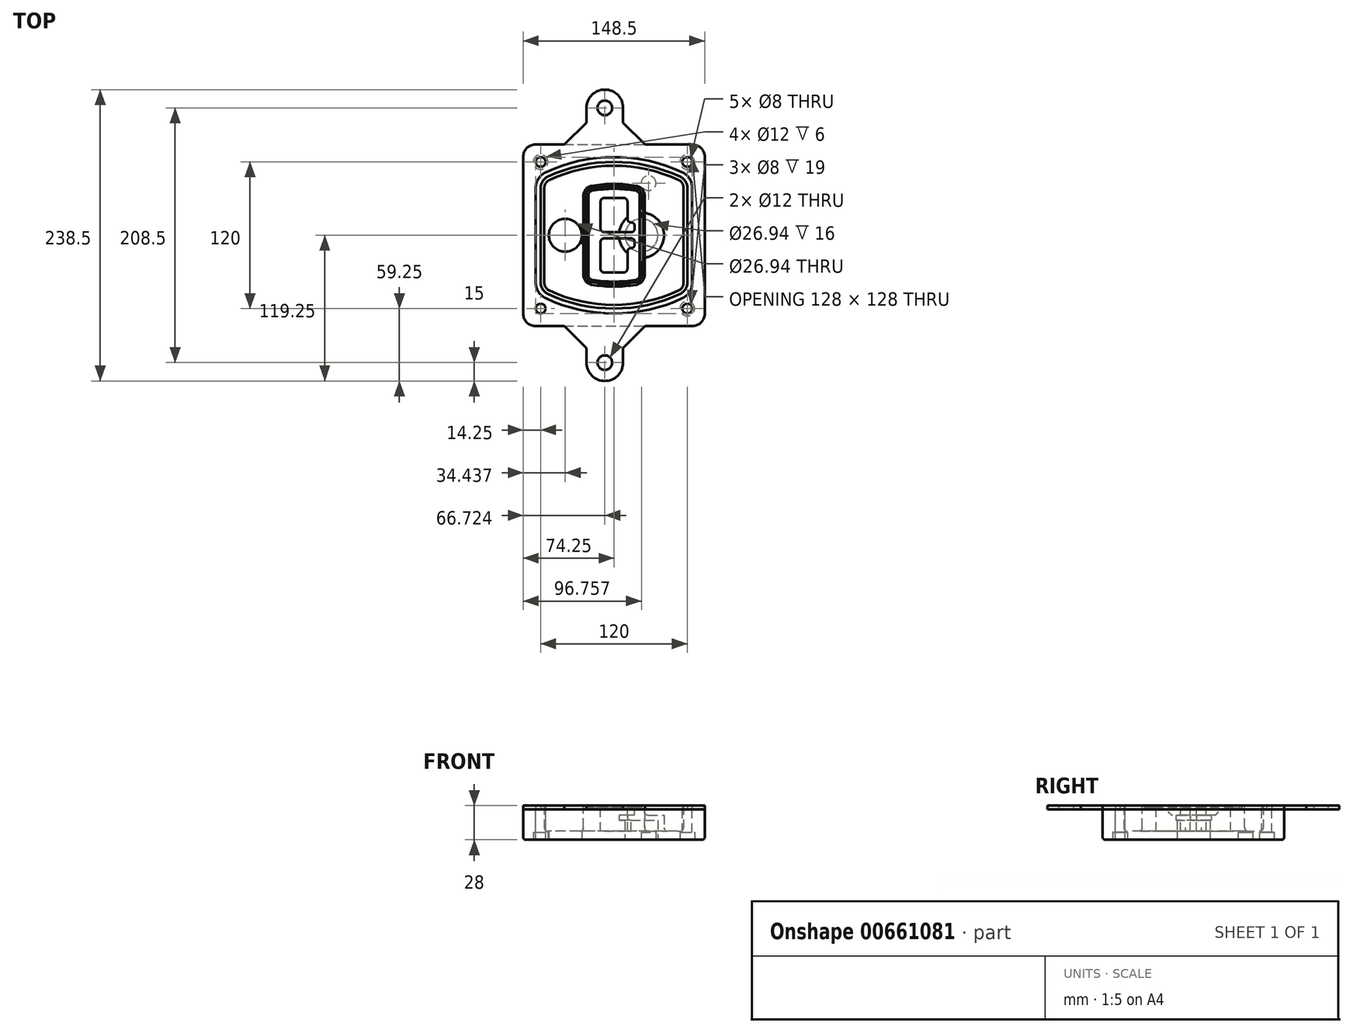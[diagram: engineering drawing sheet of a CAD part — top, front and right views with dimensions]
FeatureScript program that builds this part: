
annotation { "Feature Type Name" : "Feature", "Feature Type Description" : "" }
export const myFeature = defineFeature(function(context is Context, id is Id, definition is map)
    precondition{}
    {
        {
            var Q0;
            Q0=qCreatedBy(makeId("Top.planeOp"),FACE);
            var sketch = newSketch(context, id + "F0", { "sketchPlane" : qUnion([Q0])});
            skPoint(sketch, "E0.rect.middle", {"position": v(0, 0) * mm});
            skLineSegment(sketch, "E1.bottom", {"start": v(-64.25, -74.25) * mm, "end": v(64.25, -74.25) * mm});
            skLineSegment(sketch, "E1.top", {"start": v(-64.25, 74.25) * mm, "end": v(64.25, 74.25) * mm});
            skLineSegment(sketch, "E1.left", {"start": v(-74.25, -64.25) * mm, "end": v(-74.25, 64.25) * mm});
            skLineSegment(sketch, "E1.right", {"start": v(74.25, -64.25) * mm, "end": v(74.25, 64.25) * mm});
            skLineSegment(sketch, "E2", {"start": v(-74.25, 74.25) * mm, "end": v(74.25, -74.25) * mm, "construction": true});
            skLineSegment(sketch, "E3", {"start": v(74.25, 74.25) * mm, "end": v(-74.25, -74.25) * mm, "construction": true});
            skCircle(sketch, "E4", {"center": v(-60, 60) * mm, "radius": 4 * mm});
            skCircle(sketch, "E5", {"center": v(60, 60) * mm, "radius": 4 * mm});
            skCircle(sketch, "E6", {"center": v(60, -60) * mm, "radius": 4 * mm});
            skCircle(sketch, "E7", {"center": v(-60, -60) * mm, "radius": 4 * mm});
            skLineSegment(sketch, "E8", {"start": v(-60, 60) * mm, "end": v(60, 60) * mm, "construction": true});
            skLineSegment(sketch, "E9", {"start": v(60, 60) * mm, "end": v(60, -60) * mm, "construction": true});
            skLineSegment(sketch, "E10", {"start": v(60, -60) * mm, "end": v(-60, -60) * mm, "construction": true});
            skLineSegment(sketch, "E11", {"start": v(-60, -60) * mm, "end": v(-60, 60) * mm, "construction": true});
            skLineSegment(sketch, "E12", {"start": v(-60, 38.83) * mm, "end": v(-60, -38.83) * mm});
            skLineSegment(sketch, "E13", {"start": v(60, 38.83) * mm, "end": v(60, -38.83) * mm});
            skArc(sketch, "E14", {"start": v(54.26, 47.88) * mm, "mid": v(0, 60) * mm, "end": v(-54.26, 47.88) * mm});
            skArc(sketch, "E15", {"start": v(-54.26, -47.88) * mm, "mid": v(0, -60) * mm, "end": v(54.26, -47.88) * mm});
            skLineSegment(sketch, "E16", {"start": v(-60, 0) * mm, "end": v(60, 0) * mm, "construction": true});
            skPoint(sketch, "E17.visualSharp", {"position": v(-60, -45) * mm});
            skArc(sketch, "E17.filletArc", {"start": v(-60, -38.83) * mm, "mid": v(-58.44, -44.2) * mm, "end": v(-54.26, -47.88) * mm});
            skPoint(sketch, "E18.visualSharp", {"position": v(-60, 45) * mm});
            skArc(sketch, "E18.filletArc", {"start": v(-54.26, 47.88) * mm, "mid": v(-58.44, 44.2) * mm, "end": v(-60, 38.83) * mm});
            skPoint(sketch, "E19.visualSharp", {"position": v(60, 45) * mm});
            skArc(sketch, "E19.filletArc", {"start": v(60, 38.83) * mm, "mid": v(58.44, 44.2) * mm, "end": v(54.26, 47.88) * mm});
            skPoint(sketch, "E20.visualSharp", {"position": v(60, -45) * mm});
            skArc(sketch, "E20.filletArc", {"start": v(54.26, -47.88) * mm, "mid": v(58.44, -44.2) * mm, "end": v(60, -38.83) * mm});
            skPoint(sketch, "E21.visualSharp", {"position": v(-74.25, 74.25) * mm});
            skArc(sketch, "E21.filletArc", {"start": v(-64.25, 74.25) * mm, "mid": v(-71.32, 71.32) * mm, "end": v(-74.25, 64.25) * mm});
            skPoint(sketch, "E22.visualSharp", {"position": v(74.25, 74.25) * mm});
            skArc(sketch, "E22.filletArc", {"start": v(74.25, 64.25) * mm, "mid": v(71.32, 71.32) * mm, "end": v(64.25, 74.25) * mm});
            skPoint(sketch, "E23.visualSharp", {"position": v(74.25, -74.25) * mm});
            skArc(sketch, "E23.filletArc", {"start": v(64.25, -74.25) * mm, "mid": v(71.32, -71.32) * mm, "end": v(74.25, -64.25) * mm});
            skPoint(sketch, "E24.visualSharp", {"position": v(-74.25, -74.25) * mm});
            skArc(sketch, "E24.filletArc", {"start": v(-74.25, -64.25) * mm, "mid": v(-71.32, -71.32) * mm, "end": v(-64.25, -74.25) * mm});
            skArc(sketch, "E25.0", {"start": v(57, 38.83) * mm, "mid": v(55.9, 42.58) * mm, "end": v(52.98, 45.17) * mm});
            skLineSegment(sketch, "E25.1", {"start": v(57, 38.83) * mm, "end": v(57, -38.83) * mm});
            skArc(sketch, "E25.2", {"start": v(52.98, -45.17) * mm, "mid": v(55.9, -42.58) * mm, "end": v(57, -38.83) * mm});
            skArc(sketch, "E25.3", {"start": v(-52.98, -45.17) * mm, "mid": v(0, -57) * mm, "end": v(52.98, -45.17) * mm});
            skArc(sketch, "E25.4", {"start": v(-57, -38.83) * mm, "mid": v(-55.9, -42.58) * mm, "end": v(-52.98, -45.17) * mm});
            skArc(sketch, "E25.5", {"start": v(52.98, 45.17) * mm, "mid": v(0, 57) * mm, "end": v(-52.98, 45.17) * mm});
            skLineSegment(sketch, "E25.6", {"start": v(-57, 38.83) * mm, "end": v(-57, -38.83) * mm});
            skArc(sketch, "E25.7", {"start": v(-52.98, 45.17) * mm, "mid": v(-55.9, 42.58) * mm, "end": v(-57, 38.83) * mm});
            skArc(sketch, "E26.0", {"start": v(-55.96, 51.5) * mm, "mid": v(-61.82, 46.33) * mm, "end": v(-64, 38.83) * mm});
            skArc(sketch, "E26.1", {"start": v(55.96, 51.5) * mm, "mid": v(0, 64) * mm, "end": v(-55.96, 51.5) * mm});
            skArc(sketch, "E26.2", {"start": v(64, 38.83) * mm, "mid": v(61.82, 46.33) * mm, "end": v(55.96, 51.5) * mm});
            skLineSegment(sketch, "E26.3", {"start": v(64, 38.83) * mm, "end": v(64, -38.83) * mm});
            skArc(sketch, "E26.4", {"start": v(55.96, -51.5) * mm, "mid": v(61.82, -46.33) * mm, "end": v(64, -38.83) * mm});
            skLineSegment(sketch, "E26.5", {"start": v(-64, 38.83) * mm, "end": v(-64, -38.83) * mm});
            skArc(sketch, "E26.6", {"start": v(-55.96, -51.5) * mm, "mid": v(0, -64) * mm, "end": v(55.96, -51.5) * mm});
            skArc(sketch, "E26.7", {"start": v(-64, -38.83) * mm, "mid": v(-61.82, -46.33) * mm, "end": v(-55.96, -51.5) * mm});
            skLineSegment(sketch, "E27", {"start": v(-40.53, 74.25) * mm, "end": v(-22.53, 92.25) * mm});
            skLineSegment(sketch, "E28", {"start": v(25.47, 74.25) * mm, "end": v(7.47, 92.25) * mm});
            skLineSegment(sketch, "E29", {"start": v(7.47, 92.25) * mm, "end": v(7.47, 104.25) * mm});
            skLineSegment(sketch, "E30", {"start": v(-22.53, 92.25) * mm, "end": v(-22.53, 104.25) * mm});
            skArc(sketch, "E31", {"start": v(7.47, 104.25) * mm, "mid": v(-7.53, 119.25) * mm, "end": v(-22.53, 104.25) * mm});
            skCircle(sketch, "E32", {"center": v(-7.53, 104.25) * mm, "radius": 6 * mm});
            skLineSegment(sketch, "E33", {"start": v(-7.53, 104.25) * mm, "end": v(-7.53, 74.25) * mm, "construction": true});
            skLineSegment(sketch, "E34", {"start": v(-74.25, 0) * mm, "end": v(74.25, 0) * mm, "construction": true});
            skArc(sketch, "E35.MirrorCS", {"start": v(-64.25, -74.25) * mm, "mid": v(-71.32, -71.32) * mm, "end": v(-74.25, -64.25) * mm});
            skLineSegment(sketch, "E36.MirrorCS", {"start": v(-40.53, -74.25) * mm, "end": v(-22.53, -92.25) * mm});
            skLineSegment(sketch, "E37.MirrorCS", {"start": v(25.47, -74.25) * mm, "end": v(7.47, -92.25) * mm});
            skArc(sketch, "E38.MirrorCS", {"start": v(7.47, -104.25) * mm, "mid": v(-7.53, -119.25) * mm, "end": v(-22.53, -104.25) * mm});
            skCircle(sketch, "E39.MirrorC", {"center": v(-7.53, -104.25) * mm, "radius": 6 * mm});
            skLineSegment(sketch, "E40.MirrorCS", {"start": v(-7.53, -104.25) * mm, "end": v(-7.53, -74.25) * mm, "construction": true});
            skLineSegment(sketch, "E41.MirrorCS", {"start": v(-22.53, -92.25) * mm, "end": v(-22.53, -104.25) * mm});
            skLineSegment(sketch, "E42.MirrorCS", {"start": v(7.47, -92.25) * mm, "end": v(7.47, -104.25) * mm});
            skSolve(sketch);
        }
        {
            var Q0;
            Q0=makeQuery(id+"F0.imprint","IMPRINT",FACE,{"disambiguationData":[TD([[makeQuery(id+"F0.imprint","IMPRINT",EDGE,{"derivedFrom":sQuery(id+"F0.wireOp",EDGE,"E1.bottom")}),1.0]])]});
            var Q1;
            Q1=makeQuery(id+"F0.imprint","IMPRINT",FACE,{"disambiguationData":[TD([[makeQuery(id+"F0.imprint","IMPRINT",EDGE,{"derivedFrom":sQuery(id+"F0.wireOp",EDGE,"E12")}),1.0]])]});
            var Q2;
            Q2=makeQuery(id+"F0.imprint","IMPRINT",FACE,{"disambiguationData":[TD([[makeQuery(id+"F0.imprint","IMPRINT",EDGE,{"derivedFrom":sQuery(id+"F0.wireOp",EDGE,"E25.0")}),1.0]])]});
            var Q3;
            Q3=makeQuery(id+"F0.imprint","IMPRINT",FACE,{"disambiguationData":[TD([[makeQuery(id+"F0.imprint","IMPRINT",EDGE,{"derivedFrom":sQuery(id+"F0.wireOp",EDGE,"E12")}),-1.0]])]});
            extrude(context, id + "F1", {"entities" : qUnion([Q0, Q1, Q2, Q3]), "oppositeDirection" : true, "depth" : 25 * mm});
        }
        {
            var Q0;
            Q0=makeQuery(id+"F0.imprint","IMPRINT",FACE,{"disambiguationData":[TD([[makeQuery(id+"F0.imprint","IMPRINT",EDGE,{"derivedFrom":sQuery(id+"F0.wireOp",EDGE,"E12")}),1.0]])]});
            extrude(context, id + "F2", {"entities" : qUnion([Q0]), "operationType" : NewBodyOperationType.ADD, "depth" : 3 * mm});
        }
        {
            var Q0;
            Q0=makeQuery(id+"F0.imprint","IMPRINT",FACE,{"disambiguationData":[TD([[makeQuery(id+"F0.imprint","IMPRINT",EDGE,{"derivedFrom":sQuery(id+"F0.wireOp",EDGE,"E25.0")}),1.0]])]});
            extrude(context, id + "F3", {"entities" : qUnion([Q0]), "operationType" : NewBodyOperationType.REMOVE, "oppositeDirection" : true, "depth" : 18 * mm});
        }
        {
            var Q0;
            Q0=makeQuery(id+"F2.opExtrude","CAP_FACE",FACE,{"disambiguationData":[OSD([sQuery(id+"F0.wireOp",EDGE,"E12"),sQuery(id+"F0.wireOp",EDGE,"E13"),sQuery(id+"F0.wireOp",EDGE,"E14"),sQuery(id+"F0.wireOp",EDGE,"E15"),sQuery(id+"F0.wireOp",EDGE,"E17.filletArc"),sQuery(id+"F0.wireOp",EDGE,"E18.filletArc"),sQuery(id+"F0.wireOp",EDGE,"E19.filletArc"),sQuery(id+"F0.wireOp",EDGE,"E20.filletArc"),sQuery(id+"F0.wireOp",EDGE,"E25.0"),sQuery(id+"F0.wireOp",EDGE,"E25.1"),sQuery(id+"F0.wireOp",EDGE,"E25.2"),sQuery(id+"F0.wireOp",EDGE,"E25.3"),sQuery(id+"F0.wireOp",EDGE,"E25.4"),sQuery(id+"F0.wireOp",EDGE,"E25.5"),sQuery(id+"F0.wireOp",EDGE,"E25.6"),sQuery(id+"F0.wireOp",EDGE,"E25.7")])],"isStart":false});
            var sketch = newSketch(context, id + "F4", { "sketchPlane" : qUnion([Q0])});
            skArc(sketch, "E43.0", {"start": v(-18.34, -40.45) * mm, "mid": v(0, -42) * mm, "end": v(18.34, -40.45) * mm});
            skArc(sketch, "E44.0", {"start": v(18.34, 40.45) * mm, "mid": v(0, 42) * mm, "end": v(-18.34, 40.45) * mm});
            skLineSegment(sketch, "E45", {"start": v(-25, 32.57) * mm, "end": v(-25, -32.57) * mm});
            skLineSegment(sketch, "E46", {"start": v(25, 32.57) * mm, "end": v(25, -32.57) * mm});
            skLineSegment(sketch, "E47", {"start": v(-25, 39.1) * mm, "end": v(25, 39.1) * mm, "construction": true});
            skLineSegment(sketch, "E48", {"start": v(-25, -39.1) * mm, "end": v(25, -39.1) * mm, "construction": true});
            skPoint(sketch, "E49.visualSharp", {"position": v(-25, 39.1) * mm});
            skArc(sketch, "E49.filletArc", {"start": v(-18.34, 40.45) * mm, "mid": v(-23.11, 37.73) * mm, "end": v(-25, 32.57) * mm});
            skPoint(sketch, "E50.visualSharp", {"position": v(25, 39.1) * mm});
            skArc(sketch, "E50.filletArc", {"start": v(25, 32.57) * mm, "mid": v(23.11, 37.73) * mm, "end": v(18.34, 40.45) * mm});
            skPoint(sketch, "E51.visualSharp", {"position": v(25, -39.1) * mm});
            skArc(sketch, "E51.filletArc", {"start": v(18.34, -40.45) * mm, "mid": v(23.11, -37.73) * mm, "end": v(25, -32.57) * mm});
            skPoint(sketch, "E52.visualSharp", {"position": v(-25, -39.1) * mm});
            skArc(sketch, "E52.filletArc", {"start": v(-25, -32.57) * mm, "mid": v(-23.11, -37.73) * mm, "end": v(-18.34, -40.45) * mm});
            skArc(sketch, "E53.0", {"start": v(52.98, 45.17) * mm, "mid": v(0, 57) * mm, "end": v(-52.98, 45.17) * mm});
            skArc(sketch, "E53.1", {"start": v(-52.98, 45.17) * mm, "mid": v(-55.9, 42.58) * mm, "end": v(-57, 38.83) * mm});
            skLineSegment(sketch, "E53.2", {"start": v(-57, 38.83) * mm, "end": v(-57, -38.83) * mm});
            skArc(sketch, "E53.3", {"start": v(-57, -38.83) * mm, "mid": v(-55.9, -42.58) * mm, "end": v(-52.98, -45.17) * mm});
            skArc(sketch, "E53.4", {"start": v(-52.98, -45.17) * mm, "mid": v(0, -57) * mm, "end": v(52.98, -45.17) * mm});
            skArc(sketch, "E53.5", {"start": v(52.98, -45.17) * mm, "mid": v(55.9, -42.58) * mm, "end": v(57, -38.83) * mm});
            skLineSegment(sketch, "E53.6", {"start": v(57, 38.83) * mm, "end": v(57, -38.83) * mm});
            skArc(sketch, "E53.7", {"start": v(57, 38.83) * mm, "mid": v(55.9, 42.58) * mm, "end": v(52.98, 45.17) * mm});
            skLineSegment(sketch, "E54.0", {"start": v(23, 32.57) * mm, "end": v(23, -32.57) * mm});
            skArc(sketch, "E54.1", {"start": v(18, -38.48) * mm, "mid": v(21.58, -36.44) * mm, "end": v(23, -32.57) * mm});
            skArc(sketch, "E54.2", {"start": v(-18, -38.48) * mm, "mid": v(0, -40) * mm, "end": v(18, -38.48) * mm});
            skArc(sketch, "E54.3", {"start": v(-23, -32.57) * mm, "mid": v(-21.58, -36.44) * mm, "end": v(-18, -38.48) * mm});
            skLineSegment(sketch, "E54.4", {"start": v(-23, 32.57) * mm, "end": v(-23, -32.57) * mm});
            skArc(sketch, "E54.5", {"start": v(23, 32.57) * mm, "mid": v(21.58, 36.44) * mm, "end": v(18, 38.48) * mm});
            skArc(sketch, "E54.6", {"start": v(-18, 38.48) * mm, "mid": v(-21.58, 36.44) * mm, "end": v(-23, 32.57) * mm});
            skArc(sketch, "E54.7", {"start": v(18, 38.48) * mm, "mid": v(0, 40) * mm, "end": v(-18, 38.48) * mm});
            skArc(sketch, "E55.0", {"start": v(21, 32.57) * mm, "mid": v(20.06, 35.15) * mm, "end": v(17.67, 36.5) * mm});
            skLineSegment(sketch, "E55.1", {"start": v(21, 32.57) * mm, "end": v(21, -32.57) * mm});
            skArc(sketch, "E55.2", {"start": v(17.67, -36.5) * mm, "mid": v(20.06, -35.15) * mm, "end": v(21, -32.57) * mm});
            skArc(sketch, "E55.3", {"start": v(-17.67, -36.5) * mm, "mid": v(0, -38) * mm, "end": v(17.67, -36.5) * mm});
            skArc(sketch, "E55.4", {"start": v(-21, -32.57) * mm, "mid": v(-20.06, -35.15) * mm, "end": v(-17.67, -36.5) * mm});
            skArc(sketch, "E55.5", {"start": v(17.67, 36.5) * mm, "mid": v(0, 38) * mm, "end": v(-17.67, 36.5) * mm});
            skLineSegment(sketch, "E55.6", {"start": v(-21, 32.57) * mm, "end": v(-21, -32.57) * mm});
            skArc(sketch, "E55.7", {"start": v(-17.67, 36.5) * mm, "mid": v(-20.06, 35.15) * mm, "end": v(-21, 32.57) * mm});
            skLineSegment(sketch, "E56", {"start": v(-25, 0) * mm, "end": v(25, 0) * mm, "construction": true});
            skLineSegment(sketch, "E57", {"start": v(-11, 5.5) * mm, "end": v(-11, 27.5) * mm});
            skLineSegment(sketch, "E58", {"start": v(-8, 30.5) * mm, "end": v(8, 30.5) * mm});
            skLineSegment(sketch, "E59", {"start": v(11, 27.5) * mm, "end": v(11, 13.5) * mm});
            skLineSegment(sketch, "E60", {"start": v(14, 10.5) * mm, "end": v(14, 10.5) * mm});
            skLineSegment(sketch, "E61", {"start": v(17, 7.5) * mm, "end": v(17, 5.5) * mm});
            skLineSegment(sketch, "E62", {"start": v(14, 2.5) * mm, "end": v(-8, 2.5) * mm});
            skPoint(sketch, "E63.visualSharp", {"position": v(-11, 30.5) * mm});
            skArc(sketch, "E63.filletArc", {"start": v(-8, 30.5) * mm, "mid": v(-10.12, 29.62) * mm, "end": v(-11, 27.5) * mm});
            skPoint(sketch, "E64.visualSharp", {"position": v(11, 30.5) * mm});
            skArc(sketch, "E64.filletArc", {"start": v(11, 27.5) * mm, "mid": v(10.12, 29.62) * mm, "end": v(8, 30.5) * mm});
            skPoint(sketch, "E65.visualSharp", {"position": v(11, 10.5) * mm});
            skArc(sketch, "E65.filletArc", {"start": v(11, 13.5) * mm, "mid": v(11.88, 11.38) * mm, "end": v(14, 10.5) * mm});
            skPoint(sketch, "E66.visualSharp", {"position": v(17, 10.5) * mm});
            skArc(sketch, "E66.filletArc", {"start": v(17, 7.5) * mm, "mid": v(16.12, 9.62) * mm, "end": v(14, 10.5) * mm});
            skPoint(sketch, "E67.visualSharp", {"position": v(17, 2.5) * mm});
            skArc(sketch, "E67.filletArc", {"start": v(14, 2.5) * mm, "mid": v(16.12, 3.38) * mm, "end": v(17, 5.5) * mm});
            skPoint(sketch, "E68.visualSharp", {"position": v(-11, 2.5) * mm});
            skArc(sketch, "E68.filletArc", {"start": v(-11, 5.5) * mm, "mid": v(-10.12, 3.38) * mm, "end": v(-8, 2.5) * mm});
            skLineSegment(sketch, "E69.0.MirrorCS", {"start": v(14, -2.5) * mm, "end": v(-8, -2.5) * mm});
            skArc(sketch, "E70.0.MirrorCS", {"start": v(-11, -5.5) * mm, "mid": v(-10.12, -3.38) * mm, "end": v(-8, -2.5) * mm});
            skLineSegment(sketch, "E71.0.MirrorCS", {"start": v(-11, -5.5) * mm, "end": v(-11, -27.5) * mm});
            skArc(sketch, "E72.0.MirrorCS", {"start": v(-8, -30.5) * mm, "mid": v(-10.12, -29.62) * mm, "end": v(-11, -27.5) * mm});
            skLineSegment(sketch, "E73.0.MirrorCS", {"start": v(-8, -30.5) * mm, "end": v(8, -30.5) * mm});
            skArc(sketch, "E74.0.MirrorCS", {"start": v(11, -27.5) * mm, "mid": v(10.12, -29.62) * mm, "end": v(8, -30.5) * mm});
            skLineSegment(sketch, "E75.0.MirrorCS", {"start": v(11, -27.5) * mm, "end": v(11, -13.5) * mm});
            skArc(sketch, "E76.0.MirrorCS", {"start": v(11, -13.5) * mm, "mid": v(11.88, -11.38) * mm, "end": v(14, -10.5) * mm});
            skArc(sketch, "E77.0.MirrorCS", {"start": v(17, -7.5) * mm, "mid": v(16.12, -9.62) * mm, "end": v(14, -10.5) * mm});
            skLineSegment(sketch, "E78.0.MirrorCS", {"start": v(17, -7.5) * mm, "end": v(17, -5.5) * mm});
            skArc(sketch, "E79.0.MirrorCS", {"start": v(14, -2.5) * mm, "mid": v(16.12, -3.38) * mm, "end": v(17, -5.5) * mm});
            skSolve(sketch);
        }
        {
            var Q0;
            Q0=makeQuery(id+"F4.imprint","IMPRINT",FACE,{"disambiguationData":[TD([[makeQuery(id+"F4.imprint","IMPRINT",EDGE,{"derivedFrom":sQuery(id+"F4.wireOp",EDGE,"E43.0")}),1.0]])]});
            var Q1;
            Q1=makeQuery(id+"F4.imprint","IMPRINT",FACE,{"disambiguationData":[TD([[makeQuery(id+"F4.imprint","IMPRINT",EDGE,{"derivedFrom":sQuery(id+"F4.wireOp",EDGE,"E54.0")}),-1.0]])]});
            var Q2;
            Q2=makeQuery(id+"F4.imprint","IMPRINT",FACE,{"disambiguationData":[TD([[makeQuery(id+"F4.imprint","IMPRINT",EDGE,{"derivedFrom":sQuery(id+"F4.wireOp",EDGE,"E55.0")}),1.0]])]});
            extrude(context, id + "F5", {"entities" : qUnion([Q0, Q1, Q2]), "operationType" : NewBodyOperationType.ADD, "endBound" : BoundingType.UP_TO_NEXT, "oppositeDirection" : true, "depth" : 25 * mm});
        }
        {
            var Q0;
            Q0=makeQuery(id+"F4.imprint","IMPRINT",FACE,{"disambiguationData":[TD([[makeQuery(id+"F4.imprint","IMPRINT",EDGE,{"derivedFrom":sQuery(id+"F4.wireOp",EDGE,"E54.0")}),-1.0]])]});
            extrude(context, id + "F6", {"entities" : qUnion([Q0]), "operationType" : NewBodyOperationType.REMOVE, "oppositeDirection" : true, "depth" : 2 * mm});
        }
        {
            var Q0;
            Q0=makeQuery(id+"F1.opExtrude","CAP_FACE",FACE,{"disambiguationData":[OSD([sQuery(id+"F0.wireOp",EDGE,"E1.bottom"),sQuery(id+"F0.wireOp",EDGE,"E1.top"),sQuery(id+"F0.wireOp",EDGE,"E1.left"),sQuery(id+"F0.wireOp",EDGE,"E1.right"),sQuery(id+"F0.wireOp",EDGE,"E4"),sQuery(id+"F0.wireOp",EDGE,"E5"),sQuery(id+"F0.wireOp",EDGE,"E6"),sQuery(id+"F0.wireOp",EDGE,"E7"),sQuery(id+"F0.wireOp",EDGE,"E21.filletArc"),sQuery(id+"F0.wireOp",EDGE,"E22.filletArc"),sQuery(id+"F0.wireOp",EDGE,"E23.filletArc"),sQuery(id+"F0.wireOp",EDGE,"E24.filletArc")])],"isStart":false});
            var sketch = newSketch(context, id + "F7", { "sketchPlane" : qUnion([Q0])});
            skCircle(sketch, "E80", {"center": v(22.5, 0) * mm, "radius": 13.47 * mm});
            skCircle(sketch, "E81", {"center": v(-39.81, 0) * mm, "radius": 13.47 * mm});
            skLineSegment(sketch, "E82", {"start": v(74.25, 0) * mm, "end": v(-74.25, 0) * mm});
            skCircle(sketch, "E83", {"center": v(22.5, 0) * mm, "radius": 18.47 * mm});
            skCircle(sketch, "E84", {"center": v(60, -60) * mm, "radius": 6 * mm});
            skCircle(sketch, "E85", {"center": v(-60, -60) * mm, "radius": 6 * mm});
            skCircle(sketch, "E86", {"center": v(28.3, -42.63) * mm, "radius": 6 * mm});
            skCircle(sketch, "E87", {"center": v(60, 60) * mm, "radius": 6 * mm});
            skSolve(sketch);
        }
        {
            var Q0;
            {var subQ1=sQuery(id+"F7.wireOp",EDGE,"E82");var subQ4=sQuery(id+"F7.wireOp",EDGE,"E80");var subQ6=makeQuery(id+"F7.imprint","INTERSECT",VERTEX,{"disambiguationData":[OD(0.0)],"derivedFrom":[subQ4,subQ1]});Q0=makeQuery(id+"F7.imprint","IMPRINT",FACE,{"disambiguationData":[TD([[makeQuery(id+"F7.imprint","IMPRINT",EDGE,{"disambiguationData":[TD([[subQ6,-1.0]])],"derivedFrom":subQ4}),-1.0]])]});}
            var Q1;
            {var subQ0=sQuery(id+"F7.wireOp",EDGE,"E82");var subQ1=sQuery(id+"F7.wireOp",EDGE,"E80");var subQ3=makeQuery(id+"F7.imprint","INTERSECT",VERTEX,{"disambiguationData":[OD(0.0)],"derivedFrom":[subQ1,subQ0]});Q1=makeQuery(id+"F7.imprint","IMPRINT",FACE,{"disambiguationData":[TD([[makeQuery(id+"F7.imprint","IMPRINT",EDGE,{"disambiguationData":[TD([[subQ3,-1.0]])],"derivedFrom":subQ1}),1.0]])]});}
            var Q2;
            {var subQ0=sQuery(id+"F7.wireOp",EDGE,"E82");var subQ1=sQuery(id+"F7.wireOp",EDGE,"E80");var subQ3=makeQuery(id+"F7.imprint","INTERSECT",VERTEX,{"disambiguationData":[OD(0.0)],"derivedFrom":[subQ1,subQ0]});Q2=makeQuery(id+"F7.imprint","IMPRINT",FACE,{"disambiguationData":[TD([[makeQuery(id+"F7.imprint","IMPRINT",EDGE,{"disambiguationData":[TD([[subQ3,1.0]])],"derivedFrom":subQ1}),1.0]])]});}
            var Q3;
            {var subQ1=sQuery(id+"F7.wireOp",EDGE,"E82");var subQ4=sQuery(id+"F7.wireOp",EDGE,"E80");var subQ6=makeQuery(id+"F7.imprint","INTERSECT",VERTEX,{"disambiguationData":[OD(0.0)],"derivedFrom":[subQ4,subQ1]});Q3=makeQuery(id+"F7.imprint","IMPRINT",FACE,{"disambiguationData":[TD([[makeQuery(id+"F7.imprint","IMPRINT",EDGE,{"disambiguationData":[TD([[subQ6,1.0]])],"derivedFrom":subQ4}),-1.0]])]});}
            extrude(context, id + "F8", {"entities" : qUnion([Q0, Q1, Q2, Q3]), "operationType" : NewBodyOperationType.ADD, "oppositeDirection" : true, "depth" : 20 * mm});
        }
        {
            var Q0;
            {var subQ0=sQuery(id+"F7.wireOp",EDGE,"E82");var subQ1=sQuery(id+"F7.wireOp",EDGE,"E80");var subQ3=makeQuery(id+"F7.imprint","INTERSECT",VERTEX,{"disambiguationData":[OD(0.0)],"derivedFrom":[subQ1,subQ0]});Q0=makeQuery(id+"F7.imprint","IMPRINT",FACE,{"disambiguationData":[TD([[makeQuery(id+"F7.imprint","IMPRINT",EDGE,{"disambiguationData":[TD([[subQ3,-1.0]])],"derivedFrom":subQ1}),1.0]])]});}
            var Q1;
            {var subQ0=sQuery(id+"F7.wireOp",EDGE,"E82");var subQ1=sQuery(id+"F7.wireOp",EDGE,"E80");var subQ3=makeQuery(id+"F7.imprint","INTERSECT",VERTEX,{"disambiguationData":[OD(0.0)],"derivedFrom":[subQ1,subQ0]});Q1=makeQuery(id+"F7.imprint","IMPRINT",FACE,{"disambiguationData":[TD([[makeQuery(id+"F7.imprint","IMPRINT",EDGE,{"disambiguationData":[TD([[subQ3,1.0]])],"derivedFrom":subQ1}),1.0]])]});}
            extrude(context, id + "F9", {"entities" : qUnion([Q0, Q1]), "operationType" : NewBodyOperationType.REMOVE, "oppositeDirection" : true, "depth" : 16 * mm});
        }
        {
            var Q0;
            {var subQ0=sQuery(id+"F7.wireOp",EDGE,"E82");var subQ1=sQuery(id+"F7.wireOp",EDGE,"E81");var subQ3=makeQuery(id+"F7.imprint","INTERSECT",VERTEX,{"disambiguationData":[OD(0.0)],"derivedFrom":[subQ1,subQ0]});Q0=makeQuery(id+"F7.imprint","IMPRINT",FACE,{"disambiguationData":[TD([[makeQuery(id+"F7.imprint","IMPRINT",EDGE,{"disambiguationData":[TD([[subQ3,-1.0]])],"derivedFrom":subQ1}),1.0]])]});}
            var Q1;
            {var subQ0=sQuery(id+"F7.wireOp",EDGE,"E82");var subQ1=sQuery(id+"F7.wireOp",EDGE,"E81");var subQ3=makeQuery(id+"F7.imprint","INTERSECT",VERTEX,{"disambiguationData":[OD(0.0)],"derivedFrom":[subQ1,subQ0]});Q1=makeQuery(id+"F7.imprint","IMPRINT",FACE,{"disambiguationData":[TD([[makeQuery(id+"F7.imprint","IMPRINT",EDGE,{"disambiguationData":[TD([[subQ3,1.0]])],"derivedFrom":subQ1}),1.0]])]});}
            extrude(context, id + "F10", {"entities" : qUnion([Q0, Q1]), "operationType" : NewBodyOperationType.REMOVE, "oppositeDirection" : true, "depth" : 25 * mm});
        }
        {
            var Q0;
            Q0=makeQuery(id+"F7.imprint","IMPRINT",FACE,{"disambiguationData":[TD([[makeQuery(id+"F7.imprint","IMPRINT",EDGE,{"derivedFrom":sQuery(id+"F7.wireOp",EDGE,"E84")}),1.0]])]});
            var Q1;
            Q1=makeQuery(id+"F7.imprint","IMPRINT",FACE,{"disambiguationData":[TD([[makeQuery(id+"F7.imprint","IMPRINT",EDGE,{"derivedFrom":makeQuery(id+"F1.opExtrude","CAP_EDGE",EDGE,{"disambiguationData":[OSD([sQuery(id+"F0.wireOp",EDGE,"E5")])],"isStart":false})}),-1.0]])]});
            var Q2;
            Q2=makeQuery(id+"F7.imprint","IMPRINT",FACE,{"disambiguationData":[TD([[makeQuery(id+"F7.imprint","IMPRINT",EDGE,{"derivedFrom":sQuery(id+"F7.wireOp",EDGE,"E85")}),1.0]])]});
            var Q3;
            Q3=makeQuery(id+"F7.imprint","IMPRINT",FACE,{"disambiguationData":[TD([[makeQuery(id+"F7.imprint","IMPRINT",EDGE,{"derivedFrom":makeQuery(id+"F1.opExtrude","CAP_EDGE",EDGE,{"disambiguationData":[OSD([sQuery(id+"F0.wireOp",EDGE,"E4")])],"isStart":false})}),-1.0]])]});
            var Q4;
            Q4=makeQuery(id+"F7.imprint","IMPRINT",FACE,{"disambiguationData":[TD([[makeQuery(id+"F7.imprint","IMPRINT",EDGE,{"derivedFrom":sQuery(id+"F7.wireOp",EDGE,"E86")}),1.0]])]});
            var Q5;
            Q5=makeQuery(id+"F7.imprint","IMPRINT",FACE,{"disambiguationData":[TD([[makeQuery(id+"F7.imprint","IMPRINT",EDGE,{"derivedFrom":makeQuery(id+"F1.opExtrude","CAP_EDGE",EDGE,{"disambiguationData":[OSD([sQuery(id+"F0.wireOp",EDGE,"E7")])],"isStart":false})}),-1.0]])]});
            var Q6;
            Q6=makeQuery(id+"F7.imprint","IMPRINT",FACE,{"disambiguationData":[TD([[makeQuery(id+"F7.imprint","IMPRINT",EDGE,{"derivedFrom":sQuery(id+"F7.wireOp",EDGE,"E87")}),1.0]])]});
            var Q7;
            Q7=makeQuery(id+"F7.imprint","IMPRINT",FACE,{"disambiguationData":[TD([[makeQuery(id+"F7.imprint","IMPRINT",EDGE,{"derivedFrom":makeQuery(id+"F1.opExtrude","CAP_EDGE",EDGE,{"disambiguationData":[OSD([sQuery(id+"F0.wireOp",EDGE,"E6")])],"isStart":false})}),-1.0]])]});
            extrude(context, id + "F11", {"entities" : qUnion([Q0, Q1, Q2, Q3, Q4, Q5, Q6, Q7]), "operationType" : NewBodyOperationType.REMOVE, "oppositeDirection" : true, "depth" : 6 * mm});
        }
        {
            var Q0;
            Q0=makeQuery(id+"F9.boolean.opBoolean","COPY",FACE,{"derivedFrom":makeQuery(id+"F9.opExtrude","CAP_FACE",FACE,{"disambiguationData":[OSD([sQuery(id+"F7.wireOp",EDGE,"E80")])],"isStart":false})});
            var sketch = newSketch(context, id + "F12", { "sketchPlane" : qUnion([Q0])});
            skArc(sketch, "E88.0", {"start": v(11, 14.45) * mm, "mid": v(6.45, 9.13) * mm, "end": v(4.2, 2.5) * mm});
            skArc(sketch, "E88.1", {"start": v(4.2, -2.5) * mm, "mid": v(6.45, -9.13) * mm, "end": v(11, -14.45) * mm});
            skLineSegment(sketch, "E89", {"start": v(4.2, -2.5) * mm, "end": v(14, -2.5) * mm});
            skLineSegment(sketch, "E90.0", {"start": v(14, 2.5) * mm, "end": v(4.2, 2.5) * mm});
            skArc(sketch, "E90.1", {"start": v(14, 2.5) * mm, "mid": v(16.12, 3.38) * mm, "end": v(17, 5.5) * mm});
            skLineSegment(sketch, "E90.2", {"start": v(17, 7.5) * mm, "end": v(17, 5.5) * mm});
            skArc(sketch, "E90.3", {"start": v(17, 7.5) * mm, "mid": v(16.12, 9.62) * mm, "end": v(14, 10.5) * mm});
            skArc(sketch, "E90.4", {"start": v(11, 13.5) * mm, "mid": v(11.88, 11.38) * mm, "end": v(14, 10.5) * mm});
            skLineSegment(sketch, "E90.5", {"start": v(11, 14.45) * mm, "end": v(11, 13.5) * mm});
            skLineSegment(sketch, "E90.7", {"start": v(14, -2.5) * mm, "end": v(4.2, -2.5) * mm});
            skArc(sketch, "E90.8", {"start": v(14, -2.5) * mm, "mid": v(16.12, -3.38) * mm, "end": v(17, -5.5) * mm});
            skLineSegment(sketch, "E90.9", {"start": v(17, -7.5) * mm, "end": v(17, -5.5) * mm});
            skArc(sketch, "E90.10", {"start": v(17, -7.5) * mm, "mid": v(16.12, -9.62) * mm, "end": v(14, -10.5) * mm});
            skArc(sketch, "E90.11", {"start": v(11, -13.5) * mm, "mid": v(11.88, -11.38) * mm, "end": v(14, -10.5) * mm});
            skLineSegment(sketch, "E90.12", {"start": v(11, -14.45) * mm, "end": v(11, -13.5) * mm});
            skPoint(sketch, "E91.orphan", {"position": v(11, -27.5) * mm});
            skPoint(sketch, "E92.orphan", {"position": v(-8, -2.5) * mm});
            skPoint(sketch, "E93.orphan", {"position": v(-8, 2.5) * mm});
            skPoint(sketch, "E94.orphan", {"position": v(11, 27.5) * mm});
            skSolve(sketch);
        }
        {
            var Q0;
            {var subQ7=sQuery(id+"F12.wireOp",EDGE,"E88.0");var subQ14=sQuery(id+"F12.wireOp",EDGE,"E88.1");var subQ16=sQuery(id+"F12.wireOp",EDGE,"E90.1");var subQ18=sQuery(id+"F12.wireOp",EDGE,"E90.8");Q0=qUnion([makeQuery(id+"F12.imprint","IMPRINT",FACE,{"disambiguationData":[TD([[makeQuery(id+"F12.imprint","IMPRINT",EDGE,{"derivedFrom":subQ7}),1.0]])]}),makeQuery(id+"F12.imprint","IMPRINT",FACE,{"disambiguationData":[TD([[makeQuery(id+"F12.imprint","IMPRINT",EDGE,{"derivedFrom":subQ14}),1.0]])]}),makeQuery(id+"F12.imprint","IMPRINT",FACE,{"disambiguationData":[TD([[makeQuery(id+"F12.imprint","IMPRINT",EDGE,{"derivedFrom":subQ16}),1.0]])]}),makeQuery(id+"F12.imprint","IMPRINT",FACE,{"disambiguationData":[TD([[makeQuery(id+"F12.imprint","IMPRINT",EDGE,{"derivedFrom":subQ18}),-1.0]])]})]);}
            var Q1;
            Q1=makeQuery(id+"F5.boolean.opBoolean","SPLIT",FACE,{"disambiguationData":[TD([makeQuery(id+"F5.opExtrude","SWEPT_FACE",FACE,{"disambiguationData":[OSD([sQuery(id+"F4.wireOp",EDGE,"E57")])]})])],"derivedFrom":makeQuery(id+"F3.boolean.opBoolean","COPY",FACE,{"derivedFrom":makeQuery(id+"F3.opExtrude","CAP_FACE",FACE,{"disambiguationData":[OSD([sQuery(id+"F0.wireOp",EDGE,"E25.0"),sQuery(id+"F0.wireOp",EDGE,"E25.1"),sQuery(id+"F0.wireOp",EDGE,"E25.2"),sQuery(id+"F0.wireOp",EDGE,"E25.3"),sQuery(id+"F0.wireOp",EDGE,"E25.4"),sQuery(id+"F0.wireOp",EDGE,"E25.5"),sQuery(id+"F0.wireOp",EDGE,"E25.6"),sQuery(id+"F0.wireOp",EDGE,"E25.7")])],"isStart":false})})});
            extrude(context, id + "F13", {"entities" : qUnion([Q0]), "operationType" : NewBodyOperationType.REMOVE, "endBound" : BoundingType.UP_TO_SURFACE, "endBoundEntityFace" : qUnion([Q1]), "depth" : 25 * mm});
        }
        {
            var Q0;
            Q0=makeQuery(id+"F3.boolean.opBoolean","COPY",EDGE,{"derivedFrom":makeQuery(id+"F3.opExtrude","CAP_EDGE",EDGE,{"disambiguationData":[OSD([sQuery(id+"F0.wireOp",EDGE,"E25.6")])],"isStart":false})});
            var Q1;
            Q1=makeQuery(id+"F8.boolean.opBoolean","INTERSECT",EDGE,{"derivedFrom":[makeQuery(id+"F5.opExtrude","SWEPT_FACE",FACE,{"disambiguationData":[OSD([sQuery(id+"F4.wireOp",EDGE,"E46")])]}),makeQuery(id+"F8.opExtrude","CAP_FACE",FACE,{"disambiguationData":[OSD([sQuery(id+"F7.wireOp",EDGE,"E83")])],"isStart":false})]});
            var Q2;
            Q2=makeQuery(id+"F8.boolean.opBoolean","INTERSECT",EDGE,{"disambiguationData":[OD(1.0)],"derivedFrom":[makeQuery(id+"F5.opExtrude","SWEPT_FACE",FACE,{"disambiguationData":[OSD([sQuery(id+"F4.wireOp",EDGE,"E46")])]}),makeQuery(id+"F8.opExtrude","SWEPT_FACE",FACE,{"disambiguationData":[OSD([sQuery(id+"F7.wireOp",EDGE,"E83")])]})]});
            var Q3;
            {var subQ0=sQuery(id+"F4.wireOp",EDGE,"E46");Q3=makeQuery(id+"F8.boolean.opBoolean","SPLIT",EDGE,{"disambiguationData":[TD([makeQuery(id+"F5.opExtrude","SWEPT_FACE",FACE,{"disambiguationData":[OSD([sQuery(id+"F4.wireOp",EDGE,"E51.filletArc")])]})])],"derivedFrom":makeQuery(id+"F5.opExtrude","CAP_EDGE",EDGE,{"disambiguationData":[OSD([subQ0])],"isStart":false})});}
            var Q4;
            {var subQ0=sQuery(id+"F0.wireOp",EDGE,"E25.7");var subQ1=sQuery(id+"F0.wireOp",EDGE,"E25.1");var subQ2=sQuery(id+"F0.wireOp",EDGE,"E25.6");var subQ3=sQuery(id+"F0.wireOp",EDGE,"E25.5");var subQ4=sQuery(id+"F0.wireOp",EDGE,"E25.4");var subQ5=sQuery(id+"F0.wireOp",EDGE,"E25.0");var subQ6=sQuery(id+"F0.wireOp",EDGE,"E25.2");var subQ7=sQuery(id+"F0.wireOp",EDGE,"E25.3");Q4=makeQuery(id+"F8.boolean.opBoolean","INTERSECT",EDGE,{"derivedFrom":[makeQuery(id+"F5.boolean.opBoolean","SPLIT",FACE,{"disambiguationData":[TD([makeQuery(id+"F2.opExtrude","SWEPT_FACE",FACE,{"disambiguationData":[OSD([subQ5])]})])],"derivedFrom":makeQuery(id+"F3.boolean.opBoolean","COPY",FACE,{"derivedFrom":makeQuery(id+"F3.opExtrude","CAP_FACE",FACE,{"disambiguationData":[OSD([subQ5,subQ1,subQ6,subQ7,subQ4,subQ3,subQ2,subQ0])],"isStart":false})})}),makeQuery(id+"F8.opExtrude","SWEPT_FACE",FACE,{"disambiguationData":[OSD([sQuery(id+"F7.wireOp",EDGE,"E83")])]})]});}
            var Q5;
            Q5=makeQuery(id+"F8.boolean.opBoolean","INTERSECT",EDGE,{"disambiguationData":[OD(0.0)],"derivedFrom":[makeQuery(id+"F5.opExtrude","SWEPT_FACE",FACE,{"disambiguationData":[OSD([sQuery(id+"F4.wireOp",EDGE,"E46")])]}),makeQuery(id+"F8.opExtrude","SWEPT_FACE",FACE,{"disambiguationData":[OSD([sQuery(id+"F7.wireOp",EDGE,"E83")])]})]});
            fillet(context, id + "F14", {"entities" : qUnion([Q0, Q1, Q2, Q3, Q4, Q5]), "radius" : 3 * mm, "tangentPropagation" : true, "allowEdgeOverflow" : false});
        }
        {
            var Q0;
            Q0=makeQuery(id+"F1.opExtrude","CAP_EDGE",EDGE,{"disambiguationData":[OSD([sQuery(id+"F0.wireOp",EDGE,"E1.bottom")])],"isStart":false});
            fillet(context, id + "F15", {"entities" : qUnion([Q0]), "radius" : 2 * mm, "tangentPropagation" : true, "allowEdgeOverflow" : false});
        }
        {
            var Q0;
            {var subQ0=sQuery(id+"F0.wireOp",EDGE,"E27");Q0=makeQuery(id+"F0.imprint","IMPRINT",FACE,{"disambiguationData":[TD([[makeQuery(id+"F0.imprint","IMPRINT",EDGE,{"derivedFrom":subQ0}),-1.0]])]});}
            var Q1;
            {var subQ1=sQuery(id+"F0.wireOp",EDGE,"E36.MirrorCS");Q1=makeQuery(id+"F0.imprint","IMPRINT",FACE,{"disambiguationData":[TD([[makeQuery(id+"F0.imprint","IMPRINT",EDGE,{"derivedFrom":subQ1}),1.0]])]});}
            var Q2;
            Q2=makeQuery(id+"F0.imprint","IMPRINT",FACE,{"disambiguationData":[TD([[makeQuery(id+"F0.imprint","IMPRINT",EDGE,{"derivedFrom":sQuery(id+"F0.wireOp",EDGE,"E1.left")}),-1.0]])]});
            var Q3;
            Q3=makeQuery(id+"F2.opExtrude","CAP_FACE",FACE,{"disambiguationData":[OSD([sQuery(id+"F0.wireOp",EDGE,"E12"),sQuery(id+"F0.wireOp",EDGE,"E13"),sQuery(id+"F0.wireOp",EDGE,"E14"),sQuery(id+"F0.wireOp",EDGE,"E15"),sQuery(id+"F0.wireOp",EDGE,"E17.filletArc"),sQuery(id+"F0.wireOp",EDGE,"E18.filletArc"),sQuery(id+"F0.wireOp",EDGE,"E19.filletArc"),sQuery(id+"F0.wireOp",EDGE,"E20.filletArc"),sQuery(id+"F0.wireOp",EDGE,"E25.0"),sQuery(id+"F0.wireOp",EDGE,"E25.1"),sQuery(id+"F0.wireOp",EDGE,"E25.2"),sQuery(id+"F0.wireOp",EDGE,"E25.3"),sQuery(id+"F0.wireOp",EDGE,"E25.4"),sQuery(id+"F0.wireOp",EDGE,"E25.5"),sQuery(id+"F0.wireOp",EDGE,"E25.6"),sQuery(id+"F0.wireOp",EDGE,"E25.7")])],"isStart":false});
            extrude(context, id + "F16", {"entities" : qUnion([Q0, Q1, Q2]), "endBound" : BoundingType.UP_TO_SURFACE, "depth" : 25 * mm, "endBoundEntityFace" : qUnion([Q3]), "offsetDistance" : 25 * mm});
        }
    });
